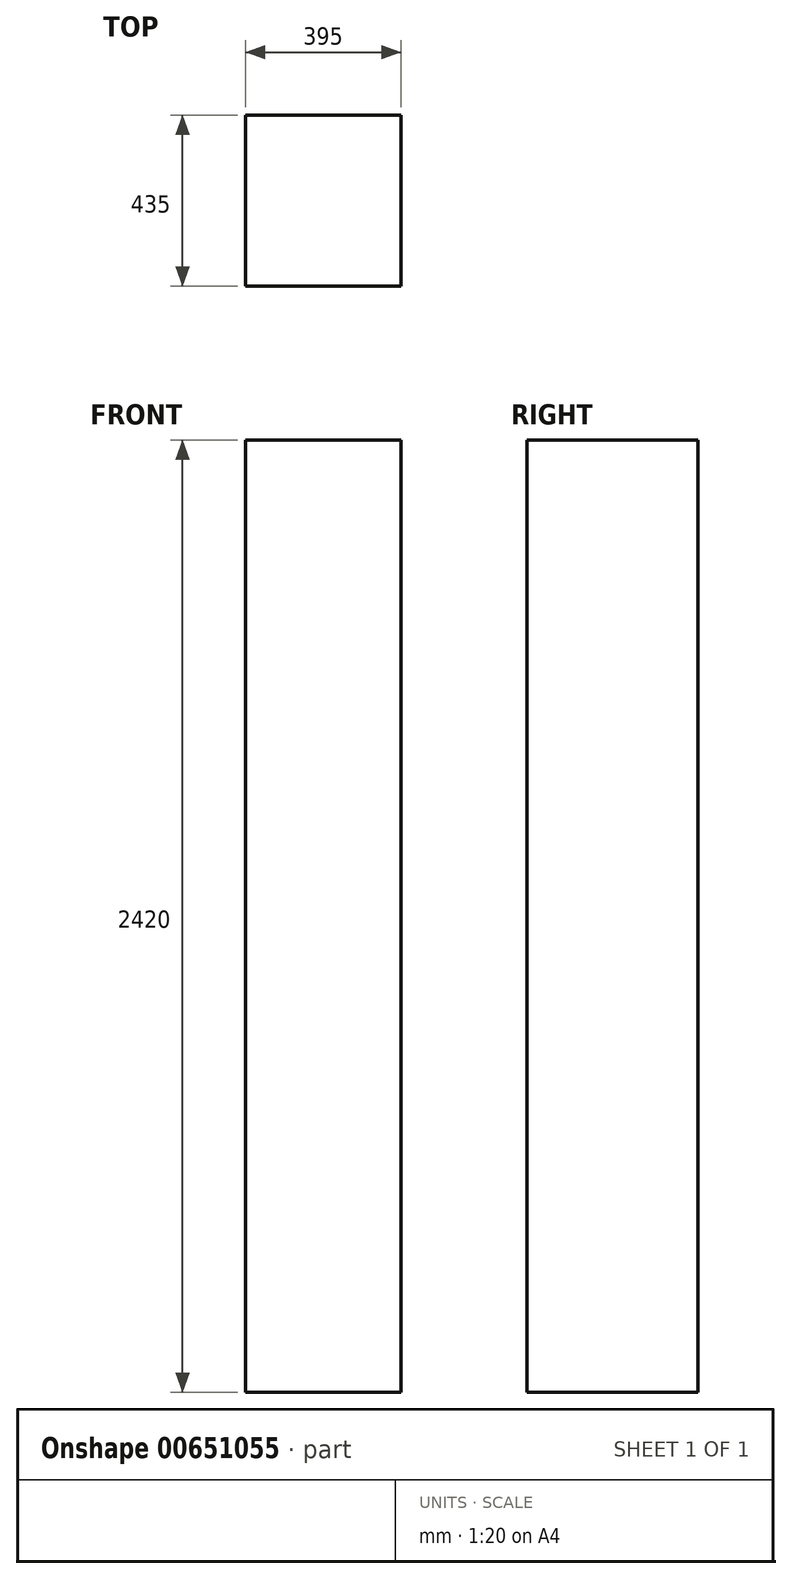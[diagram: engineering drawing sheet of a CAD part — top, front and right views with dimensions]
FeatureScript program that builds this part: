
annotation { "Feature Type Name" : "Feature", "Feature Type Description" : "" }
export const myFeature = defineFeature(function(context is Context, id is Id, definition is map)
    precondition{}
    {
        {
            var Q0;
            Q0=qCreatedBy(makeId("Top.planeOp"),FACE);
            var sketch = newSketch(context, id + "F0", { "sketchPlane" : qUnion([Q0])});
            skLineSegment(sketch, "E0.bottom", {"start": v(0, 0) * mm, "end": v(-395, 0) * mm});
            skLineSegment(sketch, "E0.top", {"start": v(0, 435) * mm, "end": v(-395, 435) * mm});
            skLineSegment(sketch, "E0.left", {"start": v(0, 0) * mm, "end": v(0, 435) * mm});
            skLineSegment(sketch, "E0.right", {"start": v(-395, 0) * mm, "end": v(-395, 435) * mm});
            skSolve(sketch);
        }
        {
            var Q0;
            Q0 = qSketchRegion(id + "F0", true);
            extrude(context, id + "F1", {"entities" : qUnion([Q0]), "depth" : 2420 * mm, "offsetDistance" : 25 * mm});
        }
    });
